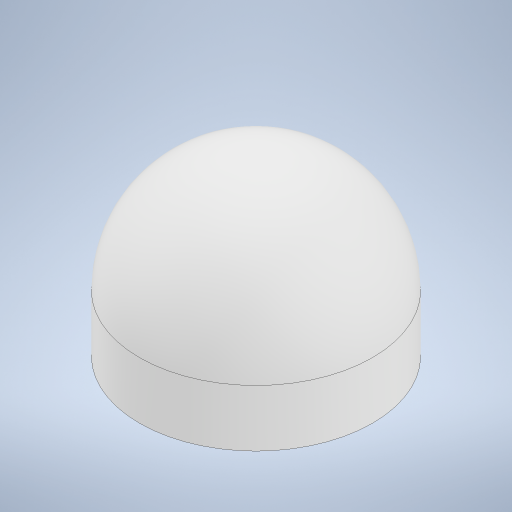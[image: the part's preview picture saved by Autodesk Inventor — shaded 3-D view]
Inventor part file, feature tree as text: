
AUTODESK INVENTOR PART (.ipt)
format: ipt  version: 2023 (Build 270158030, 158C)  size: 256,000 bytes
history: native  units: in
note: dims shown in document units (in); Inventor stores cm internally (conversion verified against a paired STEP export)
features: revolve x1, sketch x1
ambient origin geometry x8: Origin, YZ Plane, XZ Plane, XY Plane, X Axis, Y Axis, Z Axis, Center Point
bodies: Solid1 (feature_tree)
feature tree (2):
  revolve  "Revolution1"  [1 undecoded]
  sketch  "Sketch1"  dims[d1=1.5in d2=0.258in d3=90.0deg d4=2.816in]
note: 1 required parameter value undecoded (feature->parameter linkage not recoverable at this tier; creation-order binding heuristic only, values carry confidence <= 0.55)
